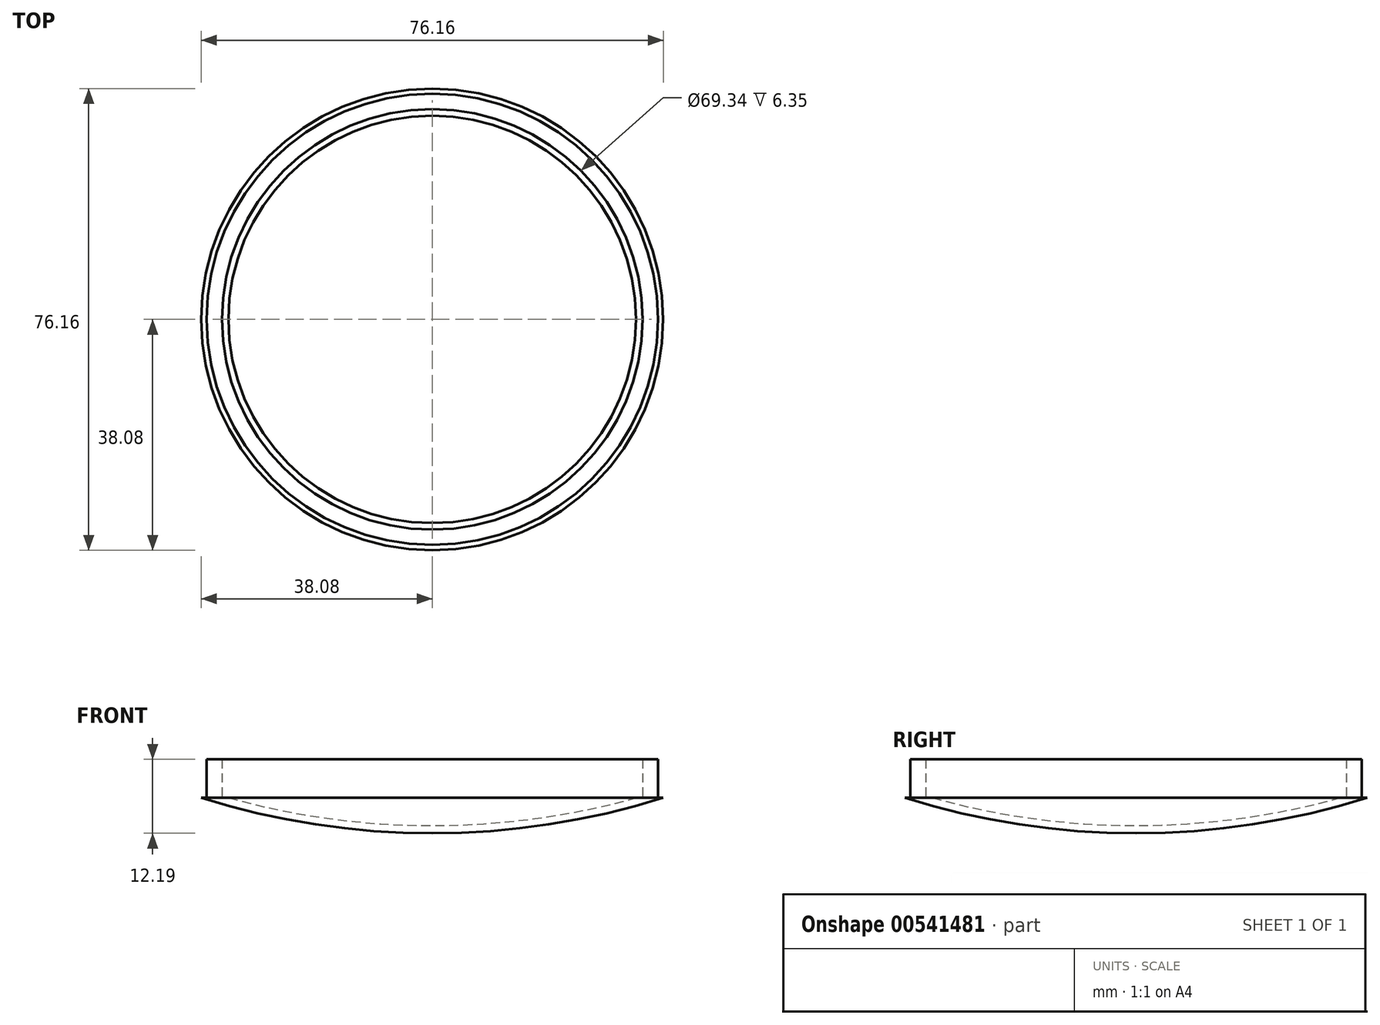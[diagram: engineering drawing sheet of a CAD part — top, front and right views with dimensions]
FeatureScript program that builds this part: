
annotation { "Feature Type Name" : "Feature", "Feature Type Description" : "" }
export const myFeature = defineFeature(function(context is Context, id is Id, definition is map)
    precondition{}
    {
        {
            var Q0;
            Q0=qCreatedBy(makeId("Top.planeOp"),FACE);
            var sketch = newSketch(context, id + "F0", { "sketchPlane" : qUnion([Q0])});
            skCircle(sketch, "E0", {"center": v(0, 0) * mm, "radius": 34.67 * mm});
            skCircle(sketch, "E1", {"center": v(0, 0) * mm, "radius": 37.21 * mm});
            skSolve(sketch);
        }
        {
            var Q0;
            Q0=qCreatedBy(makeId("Front.planeOp"),FACE);
            var sketch = newSketch(context, id + "F1", { "sketchPlane" : qUnion([Q0])});
            skLineSegment(sketch, "E2", {"start": v(-127, 121.16) * mm, "end": v(127, 121.16) * mm});
            skArc(sketch, "E3", {"start": v(127, 121.16) * mm, "mid": v(0, 248.16) * mm, "end": v(-127, 121.16) * mm});
            skSolve(sketch);
        }
        {
            var Q0;
            Q0=makeQuery(id+"F1.imprint","IMPRINT",FACE,{"disambiguationData":[TD([[makeQuery(id+"F1.imprint","IMPRINT",EDGE,{"derivedFrom":sQuery(id+"F1.wireOp",EDGE,"E2")}),1.0]])]});
            var Q1;
            Q1=sQuery(id+"F1.wireOp",EDGE,"E2");
            revolve(context, id + "F2", {"entities" : qUnion([Q0]), "axis" : qUnion([Q1]), "revolveType" : RevolveType.FULL});
        }
        {
            var Q0;
            Q0=makeQuery(id+"F2.opRevolve","SWEPT_FACE",FACE,{"disambiguationData":[OSD([sQuery(id+"F1.wireOp",EDGE,"E3")])]});
            var Q1;
            Q1=makeQuery(id+"F2.opRevolve","SWEPT_BODY",BODY,{"disambiguationData":[OSD([sQuery(id+"F1.wireOp",EDGE,"E2"),sQuery(id+"F1.wireOp",EDGE,"E3")])]});
            shell(context, id + "F3", {"isHollow" : true, "entities" : qUnion([Q0]), "parts" : qUnion([Q1]), "thickness" : 1.27 * mm});
        }
        {
            var Q0;
            Q0=qCreatedBy(makeId("Top.planeOp"),FACE);
            var sketch = newSketch(context, id + "F4", { "sketchPlane" : qUnion([Q0])});
            skLineSegment(sketch, "E4.bottom", {"start": v(-373.74, 303.05) * mm, "end": v(460.91, 303.05) * mm});
            skLineSegment(sketch, "E4.top", {"start": v(-373.74, -371.15) * mm, "end": v(460.91, -371.15) * mm});
            skLineSegment(sketch, "E4.left", {"start": v(-373.74, 303.05) * mm, "end": v(-373.74, -371.15) * mm});
            skLineSegment(sketch, "E4.right", {"start": v(460.91, 303.05) * mm, "end": v(460.91, -371.15) * mm});
            skSolve(sketch);
        }
        {
            var Q0;
            Q0=makeQuery(id+"F4.imprint","IMPRINT",FACE,{"disambiguationData":[TD([[makeQuery(id+"F4.imprint","IMPRINT",EDGE,{"derivedFrom":sQuery(id+"F4.wireOp",EDGE,"E4.bottom")}),-1.0]])]});
            extrude(context, id + "F5", {"entities" : qUnion([Q0]), "operationType" : NewBodyOperationType.REMOVE, "depth" : 508 * mm, "offsetDistance" : 25.4 * mm});
        }
        {
            var Q0;
            Q0=makeQuery(id+"F0.imprint","IMPRINT",FACE,{"disambiguationData":[TD([[makeQuery(id+"F0.imprint","IMPRINT",EDGE,{"derivedFrom":sQuery(id+"F0.wireOp",EDGE,"E0")}),-1.0]])]});
            extrude(context, id + "F6", {"entities" : qUnion([Q0]), "operationType" : NewBodyOperationType.ADD, "depth" : 6.35 * mm, "offsetDistance" : 25.4 * mm});
        }
    });
